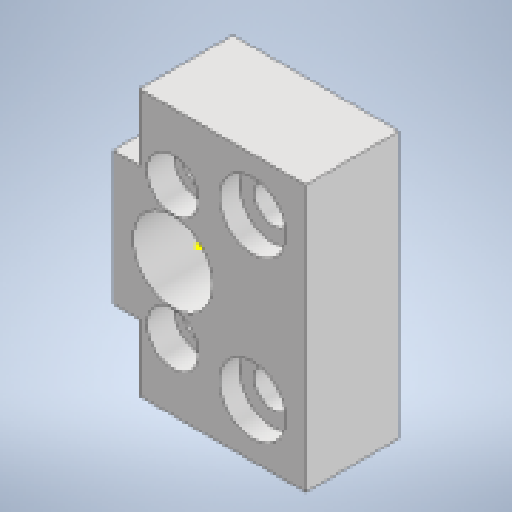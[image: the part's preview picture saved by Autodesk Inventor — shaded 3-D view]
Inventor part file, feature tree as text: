
AUTODESK INVENTOR PART (.ipt)
format: ipt  version: 2023 (Build 270158000, 158)  size: 352,768 bytes
history: native  units: mm
features: sketch x10, extrude x9, projected_geometry x4
ambient origin geometry x8: Origin, YZ Plane, XZ Plane, XY Plane, X Axis, Y Axis, Z Axis, Center Point
bodies: Solid1 (feature_tree)
feature tree (23):
  extrude  "Extrusion1"  Depth=10.0mm
  extrude  "Extrusion2"  Depth=10.0mm
  extrude  "Extrusion6"  Depth=5.0mm
  extrude  "Extrusion7"  Depth=2.4mm
  extrude  "Extrusion8"  Depth=5.0mm TaperAngle=0.0deg
  extrude  "Extrusion9"  Depth=4.0mm
  extrude  "Extrusion11"  Depth=4.0mm
  sketch  "Sketch13"  dims[d37=4.0mm d38=5.0mm]
  extrude  "Extrusion12"  Depth=5.0mm
  extrude  "Extrusion13"  Depth=5.0mm
  sketch  "Sketch1"  dims[d0=10.0mm d1=10.0mm]
  sketch  "Sketch2"  dims[d2=10.0mm d3=10.0mm]
  sketch  "Sketch7"  dims[d4=5.0mm d5=5.0mm]
  sketch  "Sketch8"  dims[d6=2.4mm d7=2.4mm]
  sketch  "Sketch9"  dims[d8=6.0mm d9=5.0mm d10=0.0mm]
  sketch  "Sketch10"  dims[d17=1.0mm d18=0.0mm d34=4.0mm]
  sketch  "Sketch12"  dims[d35=4.0mm d36=4.0mm]
  projected_geometry  "Projected Loop1"
  projected_geometry  "Projected Loop2"
  sketch  "Sketch14"  dims[d39=5.0mm d40=2.75mm]
  projected_geometry  "Projected Loop3"
  sketch  "Sketch15"  dims[d41=2.75mm d42=5.0mm d43=0.0mm d44=7.5mm d45=7.5mm d46=7.5mm d47=7.5mm d48=5.0mm d49=2.0mm d50=0.0mm d51=5.0mm d52=5.0mm d53=2.5mm d54=0.0mm d55=5.0mm d56=2.5mm d57=5.0mm d58=5.0mm d59=2.5mm d60=10.0mm d61=0.0mm d74=1.5mm d75=0.0mm d76=2.0mm d77=0.0mm d78=0.5mm d79=0.0mm d80=3.9mm d81=3.9mm d82=0.5mm d83=0.872665mm d84=0.5mm d85=0.872665mm]
  projected_geometry  "Projected Loop4"
